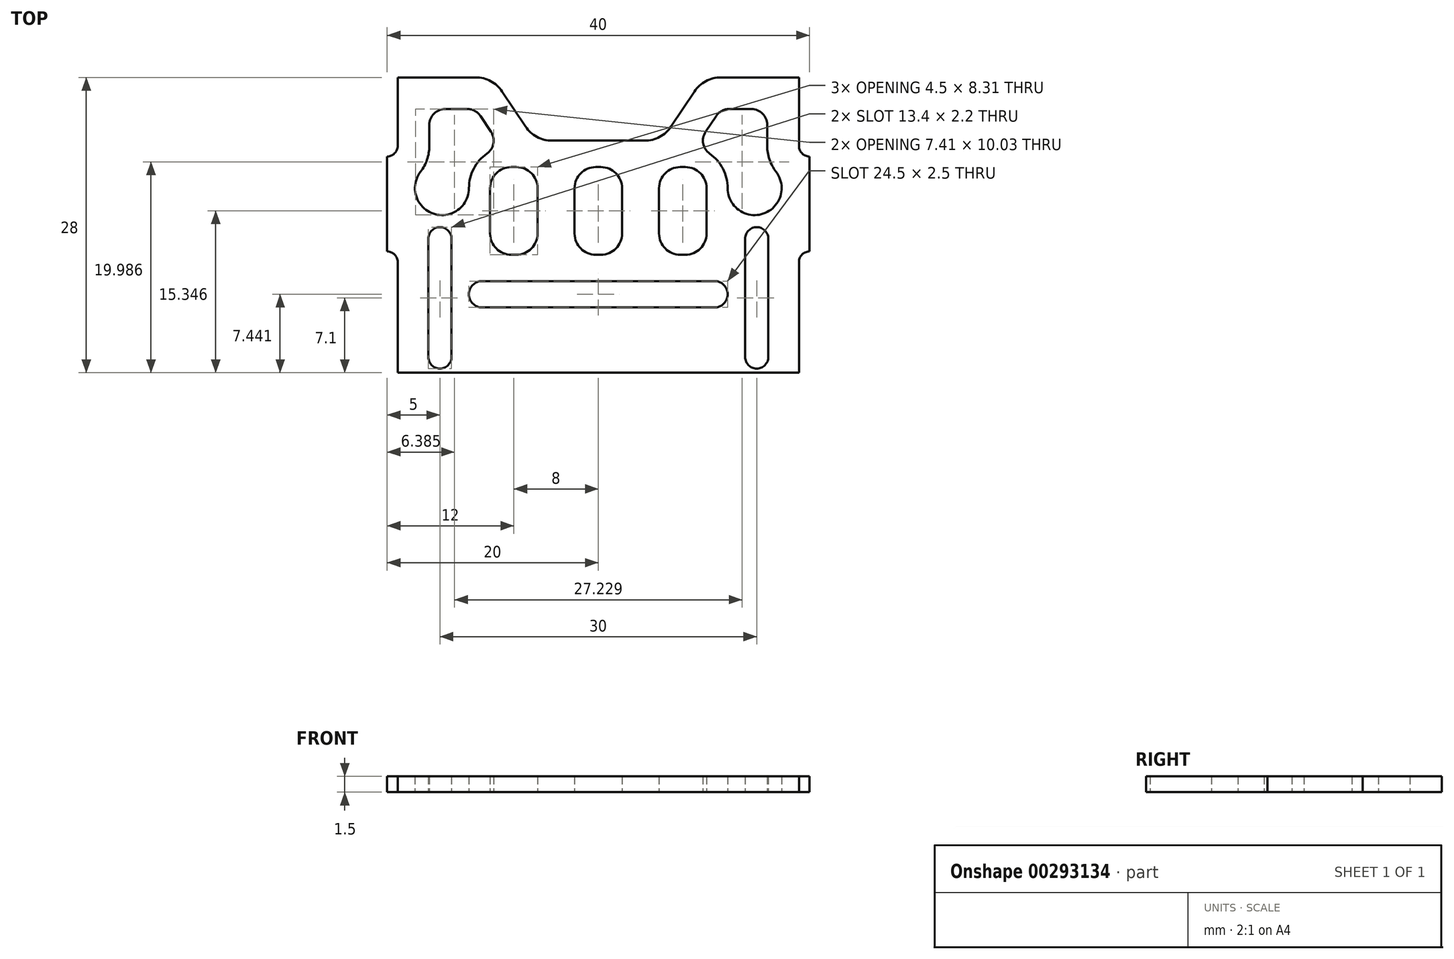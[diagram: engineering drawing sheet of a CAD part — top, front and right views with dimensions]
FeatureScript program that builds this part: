
annotation { "Feature Type Name" : "Feature", "Feature Type Description" : "" }
export const myFeature = defineFeature(function(context is Context, id is Id, definition is map)
    precondition{}
    {
        {
            var Q0;
            Q0=qCreatedBy(makeId("Top.planeOp"),FACE);
            var sketch = newSketch(context, id + "F0", { "sketchPlane" : qUnion([Q0])});
            skArc(sketch, "E0", {"start": v(19, 7.5) * mm, "mid": v(19.3, 6.8) * mm, "end": v(20, 6.5) * mm});
            skLineSegment(sketch, "E1", {"start": v(20, 6.5) * mm, "end": v(20, -2.5) * mm});
            skArc(sketch, "E2", {"start": v(20, -2.5) * mm, "mid": v(19.3, -2.8) * mm, "end": v(19, -3.5) * mm});
            skLineSegment(sketch, "E3", {"start": v(19, -3.5) * mm, "end": v(19, -14) * mm});
            skLineSegment(sketch, "E4", {"start": v(19, -14) * mm, "end": v(-19, -14) * mm});
            skLineSegment(sketch, "E5", {"start": v(-19, -14) * mm, "end": v(-19, -3.5) * mm});
            skArc(sketch, "E6", {"start": v(-19, -3.5) * mm, "mid": v(-19.3, -2.8) * mm, "end": v(-20, -2.5) * mm});
            skLineSegment(sketch, "E7", {"start": v(-20, -2.5) * mm, "end": v(-20, 6.5) * mm});
            skArc(sketch, "E8", {"start": v(-20, 6.5) * mm, "mid": v(-19.3, 6.8) * mm, "end": v(-19, 7.5) * mm});
            skLineSegment(sketch, "E9", {"start": v(-19, 7.5) * mm, "end": v(-19, 14) * mm});
            skLineSegment(sketch, "E10", {"start": v(-19, 14) * mm, "end": v(-11.6, 14) * mm});
            skArc(sketch, "E11", {"start": v(-9.1, 12.66) * mm, "mid": v(-10.19, 13.65) * mm, "end": v(-11.6, 14) * mm});
            skLineSegment(sketch, "E12", {"start": v(-9.1, 12.66) * mm, "end": v(-6.9, 9.34) * mm});
            skArc(sketch, "E13", {"start": v(-6.9, 9.34) * mm, "mid": v(-5.81, 8.35) * mm, "end": v(-4.4, 8) * mm});
            skLineSegment(sketch, "E14", {"start": v(-4.4, 8) * mm, "end": v(4.4, 8) * mm});
            skArc(sketch, "E15", {"start": v(4.4, 8) * mm, "mid": v(5.81, 8.35) * mm, "end": v(6.9, 9.34) * mm});
            skLineSegment(sketch, "E16", {"start": v(6.9, 9.34) * mm, "end": v(9.1, 12.66) * mm});
            skArc(sketch, "E17", {"start": v(11.6, 14) * mm, "mid": v(10.19, 13.65) * mm, "end": v(9.1, 12.66) * mm});
            skLineSegment(sketch, "E18", {"start": v(11.6, 14) * mm, "end": v(19, 14) * mm});
            skLineSegment(sketch, "E19", {"start": v(19, 14) * mm, "end": v(19, 7.5) * mm});
            skLineSegment(sketch, "E20", {"start": v(10.25, -0.8) * mm, "end": v(10.25, 3.5) * mm});
            skArc(sketch, "E21", {"start": v(8.25, -2.8) * mm, "mid": v(9.66, -2.22) * mm, "end": v(10.25, -0.8) * mm});
            skLineSegment(sketch, "E22", {"start": v(7.75, -2.8) * mm, "end": v(8.25, -2.8) * mm});
            skArc(sketch, "E23", {"start": v(5.75, -0.8) * mm, "mid": v(6.34, -2.22) * mm, "end": v(7.75, -2.8) * mm});
            skLineSegment(sketch, "E24", {"start": v(5.75, 3.5) * mm, "end": v(5.75, -0.8) * mm});
            skArc(sketch, "E25", {"start": v(7.75, 5.5) * mm, "mid": v(6.34, 4.91) * mm, "end": v(5.75, 3.5) * mm});
            skLineSegment(sketch, "E26", {"start": v(8.25, 5.5) * mm, "end": v(7.75, 5.5) * mm});
            skArc(sketch, "E27", {"start": v(10.25, 3.5) * mm, "mid": v(9.66, 4.91) * mm, "end": v(8.25, 5.5) * mm});
            skLineSegment(sketch, "E28", {"start": v(2.25, -0.8) * mm, "end": v(2.25, 3.5) * mm});
            skArc(sketch, "E29", {"start": v(0.25, -2.8) * mm, "mid": v(1.66, -2.22) * mm, "end": v(2.25, -0.8) * mm});
            skLineSegment(sketch, "E30", {"start": v(-0.25, -2.8) * mm, "end": v(0.25, -2.8) * mm});
            skArc(sketch, "E31", {"start": v(-2.25, -0.8) * mm, "mid": v(-1.66, -2.22) * mm, "end": v(-0.25, -2.8) * mm});
            skLineSegment(sketch, "E32", {"start": v(-2.25, 3.5) * mm, "end": v(-2.25, -0.8) * mm});
            skArc(sketch, "E33", {"start": v(-0.25, 5.5) * mm, "mid": v(-1.66, 4.91) * mm, "end": v(-2.25, 3.5) * mm});
            skLineSegment(sketch, "E34", {"start": v(0.25, 5.5) * mm, "end": v(-0.25, 5.5) * mm});
            skArc(sketch, "E35", {"start": v(2.25, 3.5) * mm, "mid": v(1.66, 4.91) * mm, "end": v(0.25, 5.5) * mm});
            skLineSegment(sketch, "E36", {"start": v(-5.75, -0.8) * mm, "end": v(-5.75, 3.5) * mm});
            skArc(sketch, "E37", {"start": v(-7.75, -2.8) * mm, "mid": v(-6.34, -2.22) * mm, "end": v(-5.75, -0.8) * mm});
            skLineSegment(sketch, "E38", {"start": v(-8.25, -2.8) * mm, "end": v(-7.75, -2.8) * mm});
            skArc(sketch, "E39", {"start": v(-10.25, -0.8) * mm, "mid": v(-9.66, -2.22) * mm, "end": v(-8.25, -2.8) * mm});
            skLineSegment(sketch, "E40", {"start": v(-10.25, 3.5) * mm, "end": v(-10.25, -0.8) * mm});
            skArc(sketch, "E41", {"start": v(-8.25, 5.5) * mm, "mid": v(-9.66, 4.91) * mm, "end": v(-10.25, 3.5) * mm});
            skLineSegment(sketch, "E42", {"start": v(-7.75, 5.5) * mm, "end": v(-8.25, 5.5) * mm});
            skArc(sketch, "E43", {"start": v(-5.75, 3.5) * mm, "mid": v(-6.34, 4.91) * mm, "end": v(-7.75, 5.5) * mm});
            skArc(sketch, "E44", {"start": v(-11, -5.3) * mm, "mid": v(-12.25, -6.56) * mm, "end": v(-11, -7.8) * mm});
            skLineSegment(sketch, "E45", {"start": v(11, -5.3) * mm, "end": v(-11, -5.3) * mm});
            skArc(sketch, "E46", {"start": v(11, -7.8) * mm, "mid": v(12.25, -6.56) * mm, "end": v(11, -5.3) * mm});
            skLineSegment(sketch, "E47", {"start": v(-11, -7.8) * mm, "end": v(11, -7.8) * mm});
            skArc(sketch, "E48", {"start": v(-16.1, -12.5) * mm, "mid": v(-15, -13.6) * mm, "end": v(-13.9, -12.5) * mm});
            skLineSegment(sketch, "E49", {"start": v(-16.1, -12.5) * mm, "end": v(-16.1, -1.3) * mm});
            skArc(sketch, "E50", {"start": v(-13.9, -1.3) * mm, "mid": v(-15, -0.2) * mm, "end": v(-16.1, -1.3) * mm});
            skLineSegment(sketch, "E51", {"start": v(-13.9, -1.3) * mm, "end": v(-13.9, -12.5) * mm});
            skArc(sketch, "E52", {"start": v(13.9, -12.5) * mm, "mid": v(15, -13.6) * mm, "end": v(16.1, -12.5) * mm});
            skLineSegment(sketch, "E53", {"start": v(16.1, -12.5) * mm, "end": v(16.1, -1.3) * mm});
            skArc(sketch, "E54", {"start": v(16.1, -1.3) * mm, "mid": v(15, -0.2) * mm, "end": v(13.9, -1.3) * mm});
            skLineSegment(sketch, "E55", {"start": v(13.9, -1.3) * mm, "end": v(13.9, -12.5) * mm});
            skArc(sketch, "E56", {"start": v(-16.83, 5.06) * mm, "mid": v(-15.63, 1.08) * mm, "end": v(-12.25, 3.5) * mm});
            skArc(sketch, "E57", {"start": v(-16.83, 5.06) * mm, "mid": v(-16.21, 6.21) * mm, "end": v(-16, 7.5) * mm});
            skLineSegment(sketch, "E58", {"start": v(-16, 7.5) * mm, "end": v(-16, 9.5) * mm});
            skArc(sketch, "E59", {"start": v(-14.5, 11) * mm, "mid": v(-15.56, 10.56) * mm, "end": v(-16, 9.5) * mm});
            skLineSegment(sketch, "E60", {"start": v(-14.5, 11) * mm, "end": v(-12.4, 11) * mm});
            skArc(sketch, "E61", {"start": v(-11.16, 10.33) * mm, "mid": v(-11.7, 10.82) * mm, "end": v(-12.4, 11) * mm});
            skLineSegment(sketch, "E62", {"start": v(-11.16, 10.33) * mm, "end": v(-10.16, 8.83) * mm});
            skArc(sketch, "E63", {"start": v(-10.55, 6.77) * mm, "mid": v(-9.94, 7.73) * mm, "end": v(-10.16, 8.83) * mm});
            skArc(sketch, "E64", {"start": v(-10.55, 6.77) * mm, "mid": v(-11.8, 5.35) * mm, "end": v(-12.25, 3.5) * mm});
            skArc(sketch, "E65", {"start": v(12.25, 3.5) * mm, "mid": v(15.63, 1.08) * mm, "end": v(16.83, 5.06) * mm});
            skArc(sketch, "E66", {"start": v(16, 7.5) * mm, "mid": v(16.21, 6.21) * mm, "end": v(16.83, 5.06) * mm});
            skLineSegment(sketch, "E67", {"start": v(16, 7.5) * mm, "end": v(16, 9.5) * mm});
            skArc(sketch, "E68", {"start": v(16, 9.5) * mm, "mid": v(15.56, 10.56) * mm, "end": v(14.5, 11) * mm});
            skLineSegment(sketch, "E69", {"start": v(14.5, 11) * mm, "end": v(12.4, 11) * mm});
            skArc(sketch, "E70", {"start": v(12.4, 11) * mm, "mid": v(11.7, 10.82) * mm, "end": v(11.16, 10.33) * mm});
            skLineSegment(sketch, "E71", {"start": v(11.16, 10.33) * mm, "end": v(10.16, 8.83) * mm});
            skArc(sketch, "E72", {"start": v(10.16, 8.83) * mm, "mid": v(9.94, 7.73) * mm, "end": v(10.55, 6.77) * mm});
            skArc(sketch, "E73", {"start": v(12.25, 3.5) * mm, "mid": v(11.8, 5.35) * mm, "end": v(10.55, 6.77) * mm});
            skSolve(sketch);
        }
        {
            var Q0;
            Q0 = qSketchRegion(id + "F0", true);
            extrude(context, id + "F1", {"entities" : qUnion([Q0]), "depth" : 1.5 * mm});
        }
    });
